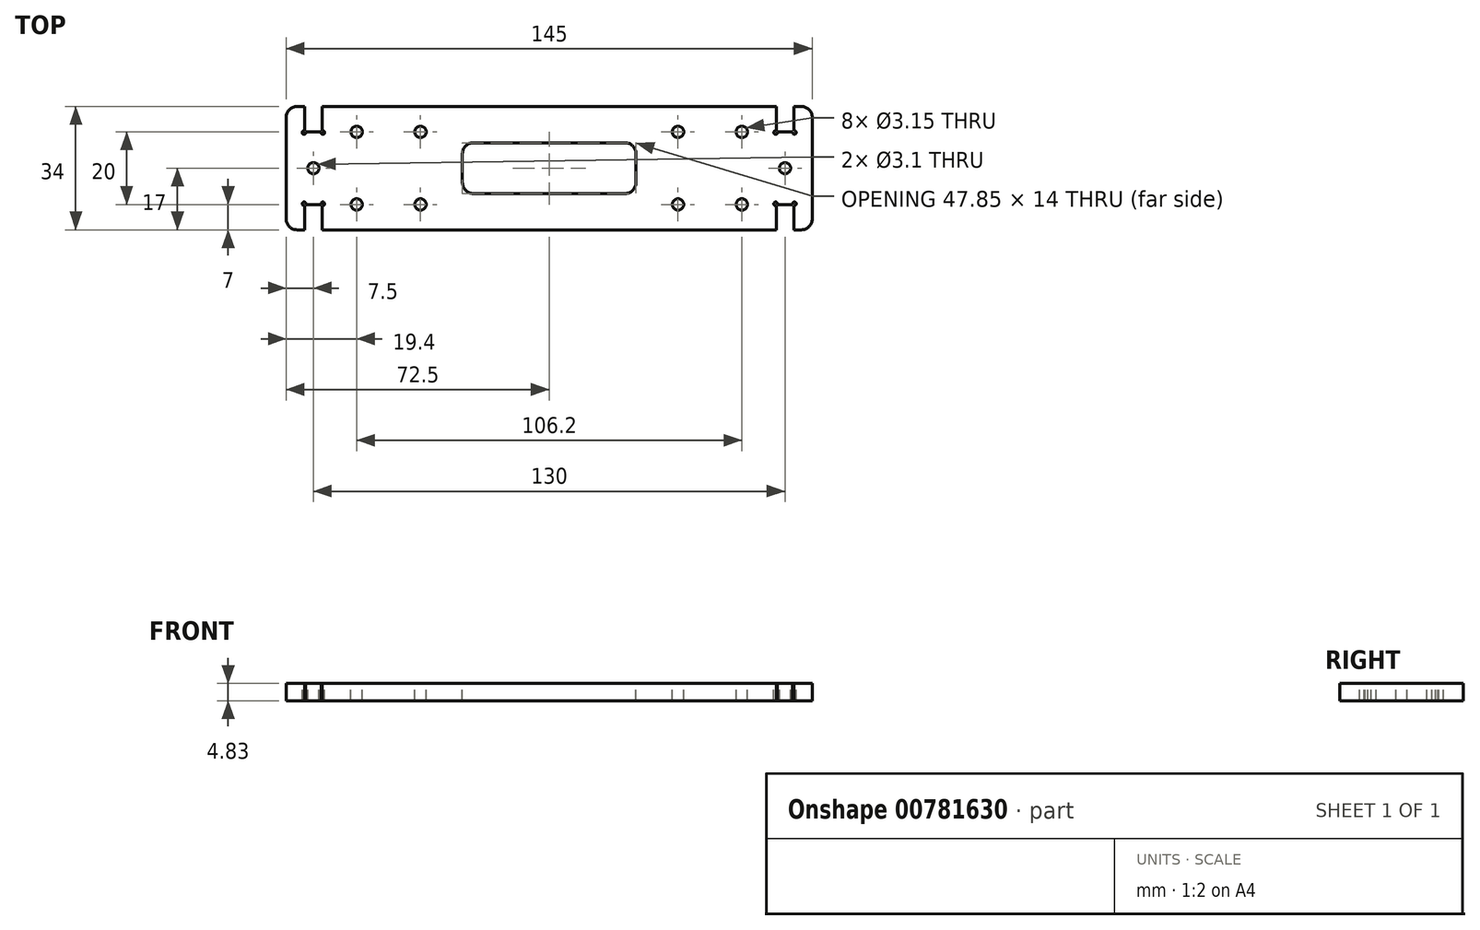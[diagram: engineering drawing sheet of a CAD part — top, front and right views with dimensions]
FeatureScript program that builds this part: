
annotation { "Feature Type Name" : "Feature", "Feature Type Description" : "" }
export const myFeature = defineFeature(function(context is Context, id is Id, definition is map)
    precondition{}
    {
        {
            var Q0;
            Q0=qCreatedBy(makeId("Top.planeOp"),FACE);
            var sketch = newSketch(context, id + "F0", { "sketchPlane" : qUnion([Q0])});
            skLineSegment(sketch, "E0.bottom", {"start": v(72.5, 17) * mm, "end": v(-72.5, 17) * mm});
            skLineSegment(sketch, "E0.top", {"start": v(72.5, -17) * mm, "end": v(-72.5, -17) * mm});
            skLineSegment(sketch, "E0.left", {"start": v(72.5, 17) * mm, "end": v(72.5, -17) * mm});
            skLineSegment(sketch, "E0.right", {"start": v(-72.5, 17) * mm, "end": v(-72.5, -17) * mm});
            skPoint(sketch, "E0.middle", {"position": v(0, 0) * mm});
            skSolve(sketch);
        }
        {
            var Q0;
            Q0=qSketchRegion(id+"F0",true);
            extrude(context, id + "F1", {"entities" : qUnion([Q0]), "depth" : 4.83 * mm, "offsetDistance" : 25 * mm});
        }
        {
            var Q0;
            Q0=makeQuery(id+"F1.opExtrude","CAP_FACE",FACE,{"disambiguationData":[OSD([sQuery(id+"F0.wireOp",EDGE,"E0.bottom"),sQuery(id+"F0.wireOp",EDGE,"E0.top"),sQuery(id+"F0.wireOp",EDGE,"E0.left"),sQuery(id+"F0.wireOp",EDGE,"E0.right")])],"isStart":false});
            var sketch = newSketch(context, id + "F2", { "sketchPlane" : qUnion([Q0])});
            skCircle(sketch, "E1", {"center": v(-53.1, -10) * mm, "radius": 1.57 * mm});
            skCircle(sketch, "E2", {"center": v(-35.5, -10) * mm, "radius": 1.57 * mm});
            skLineSegment(sketch, "E3", {"start": v(-53.1, -10) * mm, "end": v(-35.5, -10) * mm, "construction": true});
            skPoint(sketch, "E4.positionSnap0", {"position": v(-44.3, -10) * mm});
            skCircle(sketch, "E5", {"center": v(-53.1, -10) * mm, "radius": 2.3 * mm, "construction": true});
            skCircle(sketch, "E6", {"center": v(-35.5, -10) * mm, "radius": 2.3 * mm, "construction": true});
            skLineSegment(sketch, "E7", {"start": v(0, 17) * mm, "end": v(0, -17) * mm, "construction": true});
            skPoint(sketch, "E8.MirrorP", {"position": v(44.3, -10) * mm});
            skCircle(sketch, "E9.MirrorC", {"center": v(53.1, -10) * mm, "radius": 1.57 * mm});
            skCircle(sketch, "E10.MirrorC", {"center": v(35.5, -10) * mm, "radius": 1.57 * mm});
            skCircle(sketch, "E11.MirrorC", {"center": v(53.1, -10) * mm, "radius": 2.3 * mm, "construction": true});
            skCircle(sketch, "E12.MirrorC", {"center": v(35.5, -10) * mm, "radius": 2.3 * mm, "construction": true});
            skLineSegment(sketch, "E13", {"start": v(-72.5, 0) * mm, "end": v(72.5, 0) * mm, "construction": true});
            skCircle(sketch, "E14.MirrorC", {"center": v(-35.5, 10) * mm, "radius": 1.57 * mm});
            skCircle(sketch, "E15.MirrorC", {"center": v(53.1, 10) * mm, "radius": 2.3 * mm, "construction": true});
            skCircle(sketch, "E16.MirrorC", {"center": v(-35.5, 10) * mm, "radius": 2.3 * mm, "construction": true});
            skCircle(sketch, "E17.MirrorC", {"center": v(-53.1, 10) * mm, "radius": 1.57 * mm});
            skCircle(sketch, "E18.MirrorC", {"center": v(-53.1, 10) * mm, "radius": 2.3 * mm, "construction": true});
            skLineSegment(sketch, "E19.MirrorCS", {"start": v(-53.1, 10) * mm, "end": v(-35.5, 10) * mm, "construction": true});
            skPoint(sketch, "E20.MirrorP", {"position": v(44.3, 10) * mm});
            skPoint(sketch, "E21.MirrorP", {"position": v(-44.3, 10) * mm});
            skCircle(sketch, "E22.MirrorC", {"center": v(35.5, 10) * mm, "radius": 1.57 * mm});
            skCircle(sketch, "E23.MirrorC", {"center": v(35.5, 10) * mm, "radius": 2.3 * mm, "construction": true});
            skCircle(sketch, "E24.MirrorC", {"center": v(53.1, 10) * mm, "radius": 1.57 * mm});
            skSolve(sketch);
        }
        {
            var Q0;
            Q0=qSketchRegion(id+"F2",true);
            var Q1;
            Q1=makeQuery(id+"F1.opExtrude","CAP_FACE",FACE,{"disambiguationData":[OSD([sQuery(id+"F0.wireOp",EDGE,"E0.bottom"),sQuery(id+"F0.wireOp",EDGE,"E0.top"),sQuery(id+"F0.wireOp",EDGE,"E0.left"),sQuery(id+"F0.wireOp",EDGE,"E0.right")])],"isStart":true});
            extrude(context, id + "F3", {"entities" : qUnion([Q0]), "operationType" : NewBodyOperationType.REMOVE, "endBound" : BoundingType.UP_TO_SURFACE, "oppositeDirection" : true, "depth" : 25 * mm, "endBoundEntityFace" : qUnion([Q1]), "offsetDistance" : 25 * mm});
        }
        {
            var Q0;
            Q0=makeQuery(id+"F1.opExtrude","SWEPT_EDGE",EDGE,{"disambiguationData":[OSD([sQuery(id+"F0.wireOp",EDGE,"E0.top"),sQuery(id+"F0.wireOp",EDGE,"E0.right")])]});
            var Q1;
            Q1=makeQuery(id+"F1.opExtrude","SWEPT_EDGE",EDGE,{"disambiguationData":[OSD([sQuery(id+"F0.wireOp",EDGE,"E0.bottom"),sQuery(id+"F0.wireOp",EDGE,"E0.right")])]});
            var Q2;
            Q2=makeQuery(id+"F1.opExtrude","SWEPT_EDGE",EDGE,{"disambiguationData":[OSD([sQuery(id+"F0.wireOp",EDGE,"E0.top"),sQuery(id+"F0.wireOp",EDGE,"E0.left")])]});
            var Q3;
            Q3=makeQuery(id+"F1.opExtrude","SWEPT_EDGE",EDGE,{"disambiguationData":[OSD([sQuery(id+"F0.wireOp",EDGE,"E0.bottom"),sQuery(id+"F0.wireOp",EDGE,"E0.left")])]});
            fillet(context, id + "F4", {"entities" : qUnion([Q0, Q1, Q2, Q3]), "radius" : 3 * mm, "tangentPropagation" : true, "allowEdgeOverflow" : false});
        }
        {
            var Q0;
            Q0=makeQuery(id+"F1.opExtrude","CAP_FACE",FACE,{"disambiguationData":[OSD([sQuery(id+"F0.wireOp",EDGE,"E0.bottom"),sQuery(id+"F0.wireOp",EDGE,"E0.top"),sQuery(id+"F0.wireOp",EDGE,"E0.left"),sQuery(id+"F0.wireOp",EDGE,"E0.right")])],"isStart":false});
            var sketch = newSketch(context, id + "F5", { "sketchPlane" : qUnion([Q0])});
            skLineSegment(sketch, "E25", {"start": v(0, 17) * mm, "end": v(0, -17) * mm, "construction": true});
            skLineSegment(sketch, "E26.bottom", {"start": v(-67.41, 17) * mm, "end": v(-62.59, 17) * mm});
            skLineSegment(sketch, "E26.top", {"start": v(-67.41, 10) * mm, "end": v(-62.59, 10) * mm});
            skLineSegment(sketch, "E26.left", {"start": v(-67.41, 17) * mm, "end": v(-67.41, 10) * mm});
            skLineSegment(sketch, "E26.right", {"start": v(-62.59, 17) * mm, "end": v(-62.59, 10) * mm});
            skLineSegment(sketch, "E27.bottom", {"start": v(-67.41, -17) * mm, "end": v(-62.59, -17) * mm});
            skLineSegment(sketch, "E27.top", {"start": v(-67.41, -10) * mm, "end": v(-62.59, -10) * mm});
            skLineSegment(sketch, "E27.left", {"start": v(-67.41, -17) * mm, "end": v(-67.41, -10) * mm});
            skLineSegment(sketch, "E27.right", {"start": v(-62.59, -17) * mm, "end": v(-62.59, -10) * mm});
            skCircle(sketch, "E28", {"center": v(-65, 0) * mm, "radius": 1.55 * mm});
            skLineSegment(sketch, "E29", {"start": v(-65, 10) * mm, "end": v(-65, -10) * mm, "construction": true});
            skLineSegment(sketch, "E30.MirrorCS", {"start": v(67.41, -10) * mm, "end": v(62.59, -10) * mm});
            skLineSegment(sketch, "E31.MirrorCS", {"start": v(67.41, 10) * mm, "end": v(62.59, 10) * mm});
            skLineSegment(sketch, "E32.MirrorCS", {"start": v(67.41, 17) * mm, "end": v(62.59, 17) * mm});
            skLineSegment(sketch, "E33.MirrorCS", {"start": v(65, 10) * mm, "end": v(65, -10) * mm, "construction": true});
            skCircle(sketch, "E34.MirrorC", {"center": v(65, 0) * mm, "radius": 1.55 * mm});
            skLineSegment(sketch, "E35.MirrorCS", {"start": v(62.59, -17) * mm, "end": v(62.59, -10) * mm});
            skLineSegment(sketch, "E36.MirrorCS", {"start": v(67.41, -17) * mm, "end": v(67.41, -10) * mm});
            skLineSegment(sketch, "E37.MirrorCS", {"start": v(67.41, 17) * mm, "end": v(67.41, 10) * mm});
            skLineSegment(sketch, "E38.MirrorCS", {"start": v(67.41, -17) * mm, "end": v(62.59, -17) * mm});
            skLineSegment(sketch, "E39.MirrorCS", {"start": v(62.59, 17) * mm, "end": v(62.59, 10) * mm});
            skSolve(sketch);
        }
        {
            var Q0;
            Q0 = qSketchRegion(id + "F5", true);
            extrude(context, id + "F6", {"entities" : qUnion([Q0]), "operationType" : NewBodyOperationType.REMOVE, "endBound" : BoundingType.THROUGH_ALL, "oppositeDirection" : true, "depth" : 25 * mm, "offsetDistance" : 25 * mm});
        }
        {
            var Q0;
            Q0=makeQuery(id+"F1.opExtrude","CAP_FACE",FACE,{"disambiguationData":[OSD([sQuery(id+"F0.wireOp",EDGE,"E0.bottom"),sQuery(id+"F0.wireOp",EDGE,"E0.top"),sQuery(id+"F0.wireOp",EDGE,"E0.left"),sQuery(id+"F0.wireOp",EDGE,"E0.right")])],"isStart":false});
            var sketch = newSketch(context, id + "F7", { "sketchPlane" : qUnion([Q0])});
            skLineSegment(sketch, "E40", {"start": v(0, 17) * mm, "end": v(0, -17) * mm, "construction": true});
            skLineSegment(sketch, "E41", {"start": v(-72.5, 0) * mm, "end": v(72.5, 0) * mm, "construction": true});
            skLineSegment(sketch, "E42", {"start": v(-67.41, 10) * mm, "end": v(-67.59, 9.82) * mm, "construction": true});
            skCircle(sketch, "E43", {"center": v(-67.59, 9.82) * mm, "radius": 0.5 * mm});
            skLineSegment(sketch, "E44", {"start": v(-65, 10) * mm, "end": v(-65, 0) * mm, "construction": true});
            skLineSegment(sketch, "E45.MirrorCS", {"start": v(-62.59, 10) * mm, "end": v(-62.41, 9.82) * mm, "construction": true});
            skCircle(sketch, "E46.MirrorC", {"center": v(-62.41, 9.82) * mm, "radius": 0.5 * mm});
            skLineSegment(sketch, "E47.MirrorCS", {"start": v(-67.41, -10) * mm, "end": v(-67.59, -9.82) * mm, "construction": true});
            skLineSegment(sketch, "E48.MirrorCS", {"start": v(-62.59, -10) * mm, "end": v(-62.41, -9.82) * mm, "construction": true});
            skCircle(sketch, "E49.MirrorC", {"center": v(-67.59, -9.82) * mm, "radius": 0.5 * mm});
            skCircle(sketch, "E50.MirrorC", {"center": v(-62.41, -9.82) * mm, "radius": 0.5 * mm});
            skLineSegment(sketch, "E51.MirrorCS", {"start": v(67.41, 10) * mm, "end": v(67.59, 9.82) * mm, "construction": true});
            skLineSegment(sketch, "E52.MirrorCS", {"start": v(62.59, 10) * mm, "end": v(62.41, 9.82) * mm, "construction": true});
            skLineSegment(sketch, "E53.MirrorCS", {"start": v(67.41, -10) * mm, "end": v(67.59, -9.82) * mm, "construction": true});
            skLineSegment(sketch, "E54.MirrorCS", {"start": v(62.59, -10) * mm, "end": v(62.41, -9.82) * mm, "construction": true});
            skCircle(sketch, "E55.MirrorC", {"center": v(67.59, 9.82) * mm, "radius": 0.5 * mm});
            skLineSegment(sketch, "E56.MirrorCS", {"start": v(65, 10) * mm, "end": v(65, 0) * mm, "construction": true});
            skCircle(sketch, "E57.MirrorC", {"center": v(62.41, 9.82) * mm, "radius": 0.5 * mm});
            skCircle(sketch, "E58.MirrorC", {"center": v(62.41, -9.82) * mm, "radius": 0.5 * mm});
            skCircle(sketch, "E59.MirrorC", {"center": v(67.59, -9.82) * mm, "radius": 0.5 * mm});
            skSolve(sketch);
        }
        {
            var Q0;
            Q0 = qSketchRegion(id + "F7", true);
            extrude(context, id + "F8", {"entities" : qUnion([Q0]), "operationType" : NewBodyOperationType.REMOVE, "endBound" : BoundingType.THROUGH_ALL, "oppositeDirection" : true, "depth" : 25 * mm, "offsetDistance" : 25 * mm});
        }
        {
            var Q0;
            Q0=makeQuery(id+"F1.opExtrude","CAP_FACE",FACE,{"disambiguationData":[OSD([sQuery(id+"F0.wireOp",EDGE,"E0.bottom"),sQuery(id+"F0.wireOp",EDGE,"E0.top"),sQuery(id+"F0.wireOp",EDGE,"E0.left"),sQuery(id+"F0.wireOp",EDGE,"E0.right")])],"isStart":false});
            var sketch = newSketch(context, id + "F9", { "sketchPlane" : qUnion([Q0])});
            skLineSegment(sketch, "E60.bottom", {"start": v(23.93, -7) * mm, "end": v(-23.93, -7) * mm});
            skLineSegment(sketch, "E60.top", {"start": v(23.93, 7) * mm, "end": v(-23.93, 7) * mm});
            skLineSegment(sketch, "E60.left", {"start": v(23.93, -7) * mm, "end": v(23.93, 7) * mm});
            skLineSegment(sketch, "E60.right", {"start": v(-23.93, -7) * mm, "end": v(-23.93, 7) * mm});
            skPoint(sketch, "E60.middle", {"position": v(0, 0) * mm});
            skSolve(sketch);
        }
        {
            var Q0;
            Q0=makeQuery(id+"F9.imprint","IMPRINT",FACE,{"disambiguationData":[TD([[makeQuery(id+"F9.imprint","IMPRINT",EDGE,{"derivedFrom":sQuery(id+"F9.wireOp",EDGE,"E60.bottom")}),-1.0]])]});
            extrude(context, id + "F10", {"entities" : qUnion([Q0]), "operationType" : NewBodyOperationType.REMOVE, "endBound" : BoundingType.THROUGH_ALL, "oppositeDirection" : true, "depth" : 25 * mm, "offsetDistance" : 25 * mm});
        }
        {
            var Q0;
            Q0=makeQuery(id+"F10.boolean.opBoolean","COPY",EDGE,{"derivedFrom":makeQuery(id+"F10.opExtrude","SWEPT_EDGE",EDGE,{"disambiguationData":[OSD([sQuery(id+"F9.wireOp",EDGE,"E60.top"),sQuery(id+"F9.wireOp",EDGE,"E60.right")])]})});
            var Q1;
            Q1=makeQuery(id+"F10.boolean.opBoolean","COPY",EDGE,{"derivedFrom":makeQuery(id+"F10.opExtrude","SWEPT_EDGE",EDGE,{"disambiguationData":[OSD([sQuery(id+"F9.wireOp",EDGE,"E60.bottom"),sQuery(id+"F9.wireOp",EDGE,"E60.right")])]})});
            var Q2;
            Q2=makeQuery(id+"F10.boolean.opBoolean","COPY",EDGE,{"derivedFrom":makeQuery(id+"F10.opExtrude","SWEPT_EDGE",EDGE,{"disambiguationData":[OSD([sQuery(id+"F9.wireOp",EDGE,"E60.top"),sQuery(id+"F9.wireOp",EDGE,"E60.left")])]})});
            var Q3;
            Q3=makeQuery(id+"F10.boolean.opBoolean","COPY",EDGE,{"derivedFrom":makeQuery(id+"F10.opExtrude","SWEPT_EDGE",EDGE,{"disambiguationData":[OSD([sQuery(id+"F9.wireOp",EDGE,"E60.bottom"),sQuery(id+"F9.wireOp",EDGE,"E60.left")])]})});
            fillet(context, id + "F11", {"entities" : qUnion([Q0, Q1, Q2, Q3]), "radius" : 3 * mm, "tangentPropagation" : true, "allowEdgeOverflow" : false});
        }
    });
